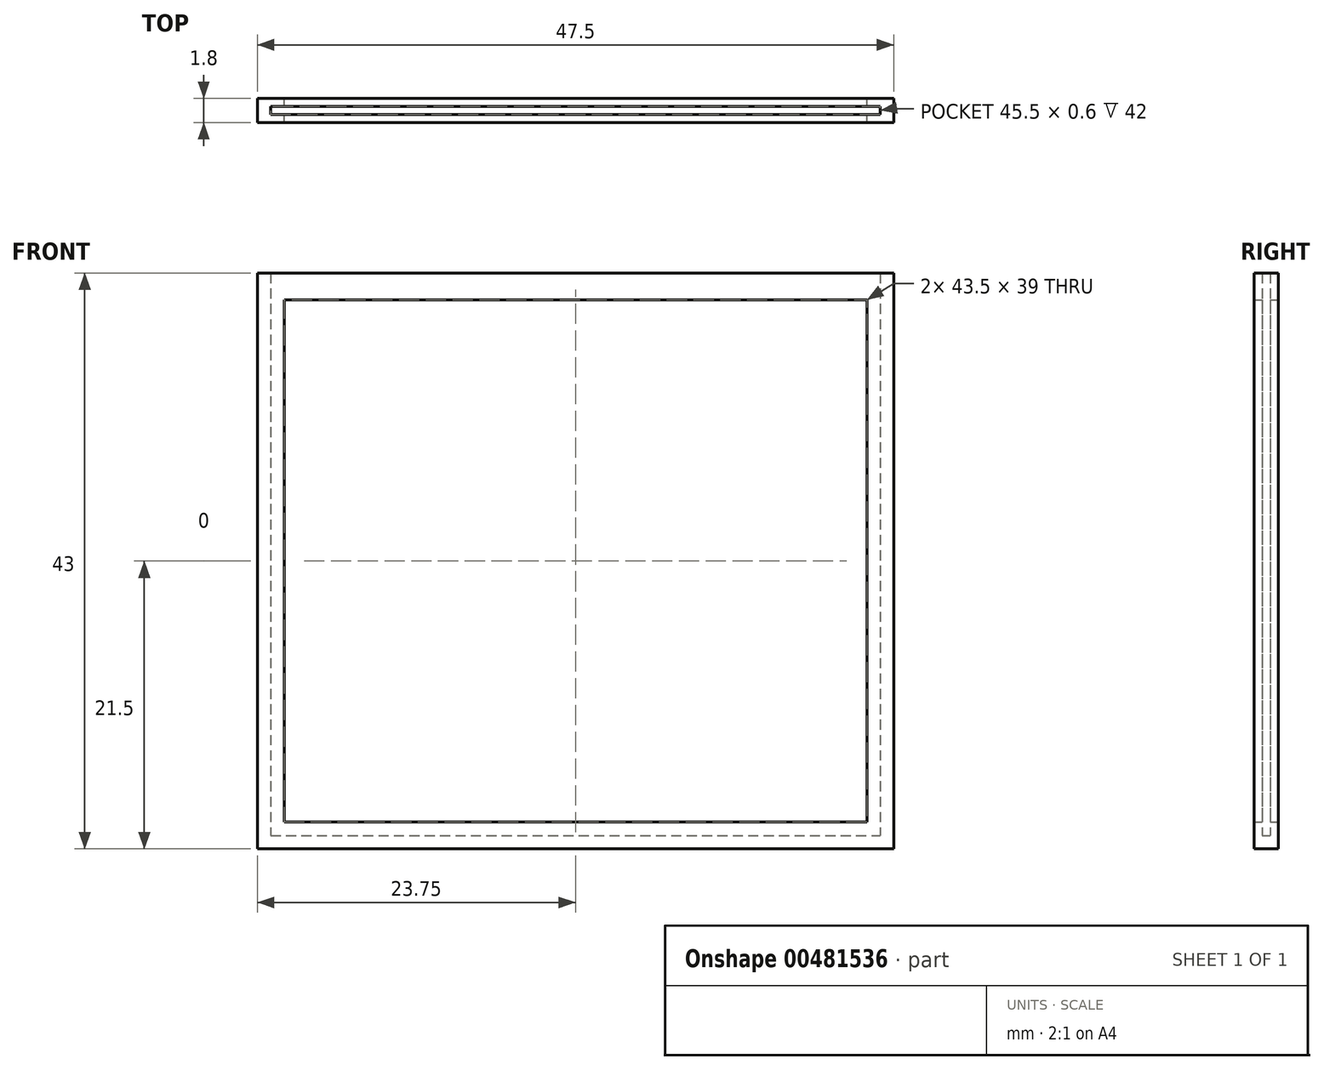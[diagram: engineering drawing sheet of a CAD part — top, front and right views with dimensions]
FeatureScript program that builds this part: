
annotation { "Feature Type Name" : "Feature", "Feature Type Description" : "" }
export const myFeature = defineFeature(function(context is Context, id is Id, definition is map)
    precondition{}
    {
        {
            var Q0;
            Q0=qCreatedBy(makeId("Front.planeOp"),FACE);
            var sketch = newSketch(context, id + "F0", { "sketchPlane" : qUnion([Q0])});
            skLineSegment(sketch, "E0.bottom", {"start": v(0, 0) * mm, "end": v(47.5, 0) * mm});
            skLineSegment(sketch, "E0.top", {"start": v(0, 43) * mm, "end": v(47.5, 43) * mm});
            skLineSegment(sketch, "E0.left", {"start": v(0, 0) * mm, "end": v(0, 43) * mm});
            skLineSegment(sketch, "E0.right", {"start": v(47.5, 0) * mm, "end": v(47.5, 43) * mm});
            skSolve(sketch);
        }
        {
            var Q0;
            Q0=makeQuery(id+"F0.imprint","IMPRINT",FACE,{"disambiguationData":[TD([[makeQuery(id+"F0.imprint","IMPRINT",EDGE,{"derivedFrom":sQuery(id+"F0.wireOp",EDGE,"E0.bottom")}),1.0]])]});
            extrude(context, id + "F1", {"entities" : qUnion([Q0]), "endBound" : BoundingType.SYMMETRIC, "depth" : 1.8 * mm});
        }
        {
            var Q0;
            Q0=qCreatedBy(makeId("Front.planeOp"),FACE);
            var sketch = newSketch(context, id + "F2", { "sketchPlane" : qUnion([Q0])});
            skLineSegment(sketch, "E1.bottom", {"start": v(2, 41) * mm, "end": v(45.5, 41) * mm});
            skLineSegment(sketch, "E1.top", {"start": v(2, 2) * mm, "end": v(45.5, 2) * mm});
            skLineSegment(sketch, "E1.left", {"start": v(2, 41) * mm, "end": v(2, 2) * mm});
            skLineSegment(sketch, "E1.right", {"start": v(45.5, 41) * mm, "end": v(45.5, 2) * mm});
            skSolve(sketch);
        }
        {
            var Q0;
            Q0 = qSketchRegion(id + "F2", true);
            extrude(context, id + "F3", {"entities" : qUnion([Q0]), "operationType" : NewBodyOperationType.REMOVE, "endBound" : BoundingType.SYMMETRIC, "depth" : 2 * mm});
        }
        {
            var Q0;
            Q0=qCreatedBy(makeId("Front.planeOp"),FACE);
            var sketch = newSketch(context, id + "F4", { "sketchPlane" : qUnion([Q0])});
            skLineSegment(sketch, "E2.bottom", {"start": v(1, 43) * mm, "end": v(46.5, 43) * mm});
            skLineSegment(sketch, "E2.top", {"start": v(1, 1) * mm, "end": v(46.5, 1) * mm});
            skLineSegment(sketch, "E2.left", {"start": v(1, 43) * mm, "end": v(1, 1) * mm});
            skLineSegment(sketch, "E2.right", {"start": v(46.5, 43) * mm, "end": v(46.5, 1) * mm});
            skSolve(sketch);
        }
        {
            var Q0;
            Q0 = qSketchRegion(id + "F4", true);
            extrude(context, id + "F5", {"entities" : qUnion([Q0]), "operationType" : NewBodyOperationType.REMOVE, "endBound" : BoundingType.SYMMETRIC, "depth" : 0.6 * mm});
        }
    });
